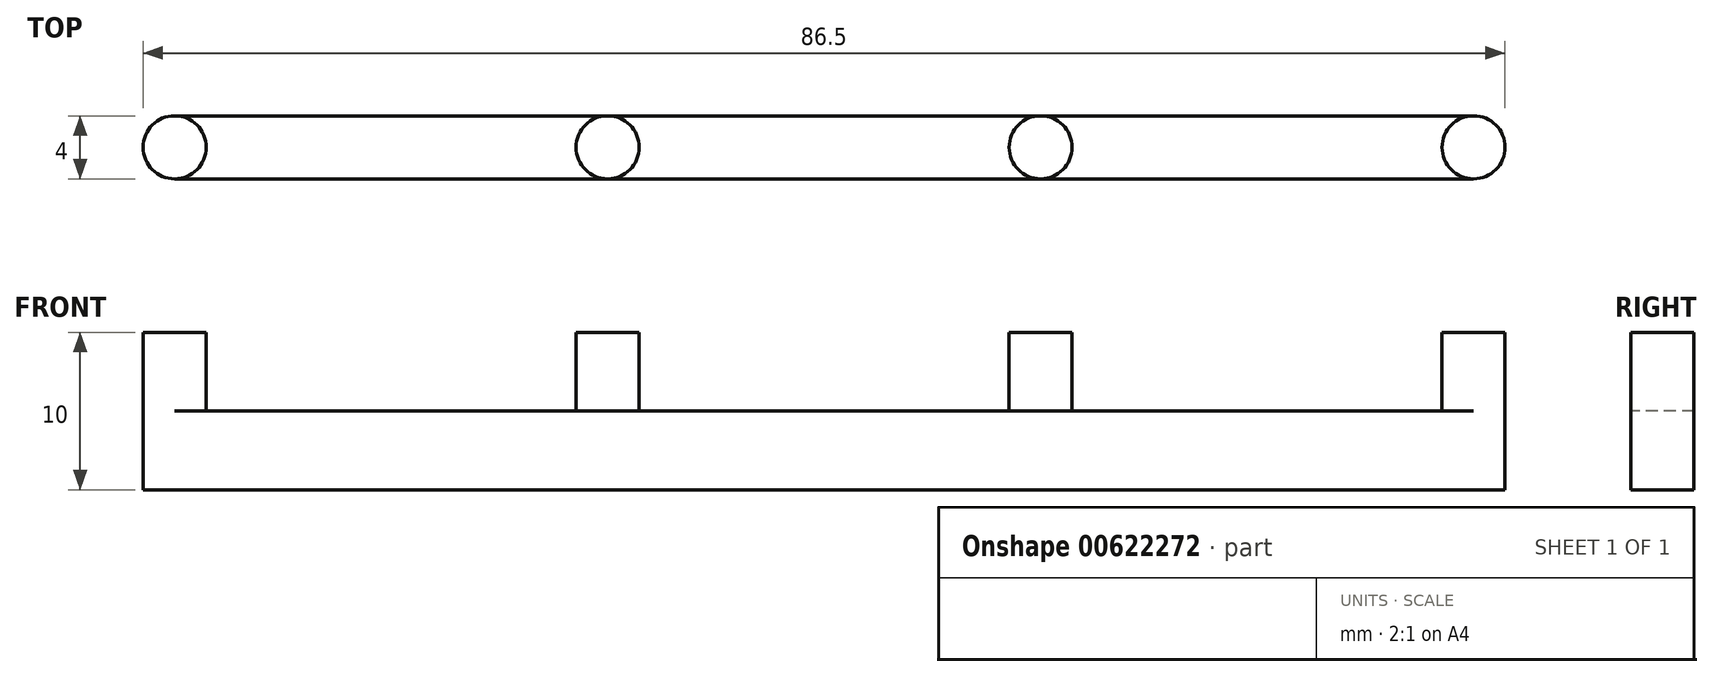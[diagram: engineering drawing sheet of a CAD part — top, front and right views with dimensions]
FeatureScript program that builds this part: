
annotation { "Feature Type Name" : "Feature", "Feature Type Description" : "" }
export const myFeature = defineFeature(function(context is Context, id is Id, definition is map)
    precondition{}
    {
        {
            var Q0;
            Q0=qCreatedBy(makeId("Top.planeOp"),FACE);
            var sketch = newSketch(context, id + "F0", { "sketchPlane" : qUnion([Q0])});
            skCircle(sketch, "E0", {"center": v(0, 0) * mm, "radius": 2 * mm});
            skLineSegment(sketch, "E1", {"start": v(0, 0) * mm, "end": v(27.5, 0) * mm});
            skLineSegment(sketch, "E2", {"start": v(27.5, 0) * mm, "end": v(55, 0) * mm});
            skLineSegment(sketch, "E3", {"start": v(55, 0) * mm, "end": v(82.5, 0) * mm});
            skCircle(sketch, "E4", {"center": v(27.5, 0) * mm, "radius": 2 * mm});
            skCircle(sketch, "E5", {"center": v(55, 0) * mm, "radius": 2 * mm});
            skCircle(sketch, "E6", {"center": v(82.5, 0) * mm, "radius": 2 * mm});
            skLineSegment(sketch, "E7.bottom", {"start": v(82.5, 2) * mm, "end": v(0, 2) * mm});
            skLineSegment(sketch, "E7.top", {"start": v(82.5, -2) * mm, "end": v(0, -2) * mm});
            skLineSegment(sketch, "E7.left", {"start": v(82.5, 2) * mm, "end": v(82.5, -2) * mm});
            skLineSegment(sketch, "E7.right", {"start": v(0, 2) * mm, "end": v(0, -2) * mm});
            skPoint(sketch, "E7.middle", {"position": v(41.25, 0) * mm});
            skSolve(sketch);
        }
        {
            var Q0;
            Q0 = qSketchRegion(id + "F0", true);
            extrude(context, id + "F1", {"entities" : qUnion([Q0]), "depth" : 5 * mm, "offsetDistance" : 25 * mm});
        }
        {
            var Q0;
            {var subQ0=sQuery(id+"F0.wireOp",EDGE,"E7.left");var subQ4=makeQuery(id+"F0.imprint","INTERSECT",VERTEX,{"derivedFrom":[sQuery(id+"F0.wireOp",EDGE,"E3"),subQ0]});Q0=makeQuery(id+"F0.imprint","IMPRINT",FACE,{"disambiguationData":[TD([[makeQuery(id+"F0.imprint","IMPRINT",EDGE,{"disambiguationData":[TD([[subQ4,1.0]])],"derivedFrom":subQ0}),1.0]])]});}
            var Q1;
            {var subQ0=sQuery(id+"F0.wireOp",EDGE,"E7.left");var subQ1=sQuery(id+"F0.wireOp",EDGE,"E3");var subQ2=makeQuery(id+"F0.imprint","INTERSECT",VERTEX,{"derivedFrom":[subQ1,subQ0]});Q1=makeQuery(id+"F0.imprint","IMPRINT",FACE,{"disambiguationData":[TD([[makeQuery(id+"F0.imprint","IMPRINT",EDGE,{"disambiguationData":[TD([[subQ2,1.0]])],"derivedFrom":subQ1}),1.0]])]});}
            var Q2;
            {var subQ0=sQuery(id+"F0.wireOp",EDGE,"E7.left");var subQ1=sQuery(id+"F0.wireOp",EDGE,"E3");var subQ2=makeQuery(id+"F0.imprint","INTERSECT",VERTEX,{"derivedFrom":[subQ1,subQ0]});Q2=makeQuery(id+"F0.imprint","IMPRINT",FACE,{"disambiguationData":[TD([[makeQuery(id+"F0.imprint","IMPRINT",EDGE,{"disambiguationData":[TD([[subQ2,1.0]])],"derivedFrom":subQ1}),-1.0]])]});}
            var Q3;
            {var subQ0=sQuery(id+"F0.wireOp",EDGE,"E3");var subQ1=sQuery(id+"F0.wireOp",EDGE,"E2");var subQ2=makeQuery(id+"F0.imprint","INTERSECT",VERTEX,{"derivedFrom":[subQ1,subQ0]});Q3=makeQuery(id+"F0.imprint","IMPRINT",FACE,{"disambiguationData":[TD([[makeQuery(id+"F0.imprint","IMPRINT",EDGE,{"disambiguationData":[TD([[subQ2,1.0]])],"derivedFrom":subQ1}),-1.0]])]});}
            var Q4;
            {var subQ0=sQuery(id+"F0.wireOp",EDGE,"E3");var subQ1=sQuery(id+"F0.wireOp",EDGE,"E2");var subQ2=makeQuery(id+"F0.imprint","INTERSECT",VERTEX,{"derivedFrom":[subQ1,subQ0]});Q4=makeQuery(id+"F0.imprint","IMPRINT",FACE,{"disambiguationData":[TD([[makeQuery(id+"F0.imprint","IMPRINT",EDGE,{"disambiguationData":[TD([[subQ2,1.0]])],"derivedFrom":subQ1}),1.0]])]});}
            var Q5;
            {var subQ0=sQuery(id+"F0.wireOp",EDGE,"E2");var subQ1=sQuery(id+"F0.wireOp",EDGE,"E1");var subQ2=makeQuery(id+"F0.imprint","INTERSECT",VERTEX,{"derivedFrom":[subQ1,subQ0]});Q5=makeQuery(id+"F0.imprint","IMPRINT",FACE,{"disambiguationData":[TD([[makeQuery(id+"F0.imprint","IMPRINT",EDGE,{"disambiguationData":[TD([[subQ2,1.0]])],"derivedFrom":subQ1}),-1.0]])]});}
            var Q6;
            {var subQ0=sQuery(id+"F0.wireOp",EDGE,"E2");var subQ1=sQuery(id+"F0.wireOp",EDGE,"E1");var subQ2=makeQuery(id+"F0.imprint","INTERSECT",VERTEX,{"derivedFrom":[subQ1,subQ0]});Q6=makeQuery(id+"F0.imprint","IMPRINT",FACE,{"disambiguationData":[TD([[makeQuery(id+"F0.imprint","IMPRINT",EDGE,{"disambiguationData":[TD([[subQ2,1.0]])],"derivedFrom":subQ1}),1.0]])]});}
            var Q7;
            {var subQ0=sQuery(id+"F0.wireOp",EDGE,"E7.right");var subQ3=sQuery(id+"F0.wireOp",EDGE,"E1");var subQ5=makeQuery(id+"F0.imprint","INTERSECT",VERTEX,{"derivedFrom":[subQ3,subQ0]});Q7=makeQuery(id+"F0.imprint","IMPRINT",FACE,{"disambiguationData":[TD([[makeQuery(id+"F0.imprint","IMPRINT",EDGE,{"disambiguationData":[TD([[subQ5,-1.0]])],"derivedFrom":subQ3}),-1.0]])]});}
            var Q8;
            {var subQ0=sQuery(id+"F0.wireOp",EDGE,"E7.right");var subQ4=makeQuery(id+"F0.imprint","INTERSECT",VERTEX,{"derivedFrom":[sQuery(id+"F0.wireOp",EDGE,"E1"),subQ0]});Q8=makeQuery(id+"F0.imprint","IMPRINT",FACE,{"disambiguationData":[TD([[makeQuery(id+"F0.imprint","IMPRINT",EDGE,{"disambiguationData":[TD([[subQ4,1.0]])],"derivedFrom":subQ0}),-1.0]])]});}
            var Q9;
            {var subQ0=sQuery(id+"F0.wireOp",EDGE,"E7.right");var subQ3=sQuery(id+"F0.wireOp",EDGE,"E1");var subQ5=makeQuery(id+"F0.imprint","INTERSECT",VERTEX,{"derivedFrom":[subQ3,subQ0]});Q9=makeQuery(id+"F0.imprint","IMPRINT",FACE,{"disambiguationData":[TD([[makeQuery(id+"F0.imprint","IMPRINT",EDGE,{"disambiguationData":[TD([[subQ5,-1.0]])],"derivedFrom":subQ3}),1.0]])]});}
            extrude(context, id + "F2", {"entities" : qUnion([Q0, Q1, Q2, Q3, Q4, Q5, Q6, Q7, Q8, Q9]), "operationType" : NewBodyOperationType.ADD, "depth" : 10 * mm, "offsetDistance" : 25 * mm});
        }
    });
